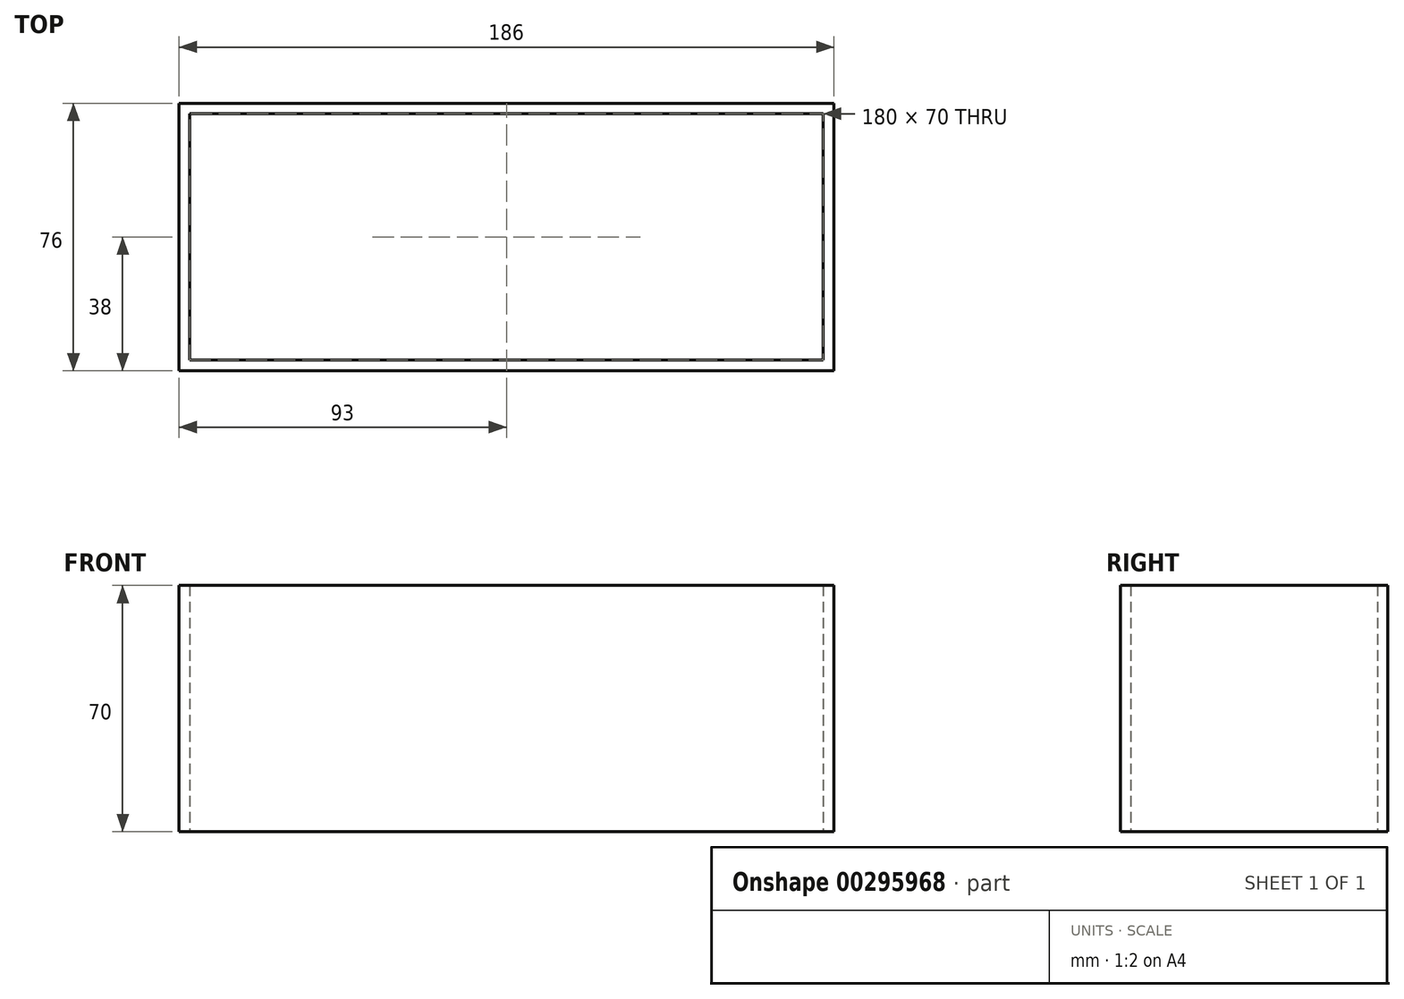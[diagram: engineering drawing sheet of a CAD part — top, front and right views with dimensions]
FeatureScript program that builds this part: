
annotation { "Feature Type Name" : "Feature", "Feature Type Description" : "" }
export const myFeature = defineFeature(function(context is Context, id is Id, definition is map)
    precondition{}
    {
        {
            var Q0;
            Q0=qCreatedBy(makeId("Top.planeOp"),FACE);
            var sketch = newSketch(context, id + "F0", { "sketchPlane" : qUnion([Q0])});
            skLineSegment(sketch, "E0", {"start": v(0, 147.07) * mm, "end": v(0, 0) * mm, "construction": true});
            skLineSegment(sketch, "E1", {"start": v(0, 0) * mm, "end": v(143.56, 0) * mm, "construction": true});
            skLineSegment(sketch, "E2.bottom", {"start": v(-90, 35) * mm, "end": v(90, 35) * mm});
            skLineSegment(sketch, "E2.top", {"start": v(-90, -35) * mm, "end": v(90, -35) * mm});
            skLineSegment(sketch, "E2.left", {"start": v(-90, 35) * mm, "end": v(-90, -35) * mm});
            skLineSegment(sketch, "E2.right", {"start": v(90, 35) * mm, "end": v(90, -35) * mm});
            skLineSegment(sketch, "E3.bottom", {"start": v(-93, 38) * mm, "end": v(93, 38) * mm});
            skLineSegment(sketch, "E3.top", {"start": v(-93, -38) * mm, "end": v(93, -38) * mm});
            skLineSegment(sketch, "E3.left", {"start": v(-93, 38) * mm, "end": v(-93, -38) * mm});
            skLineSegment(sketch, "E3.right", {"start": v(93, 38) * mm, "end": v(93, -38) * mm});
            skSolve(sketch);
        }
        {
            var Q0;
            Q0=makeQuery(id+"F0.imprint","IMPRINT",FACE,{"disambiguationData":[TD([[makeQuery(id+"F0.imprint","IMPRINT",EDGE,{"derivedFrom":sQuery(id+"F0.wireOp",EDGE,"E2.bottom")}),1.0]])]});
            extrude(context, id + "F1", {"entities" : qUnion([Q0]), "depth" : 70 * mm, "offsetDistance" : 25 * mm});
        }
    });
